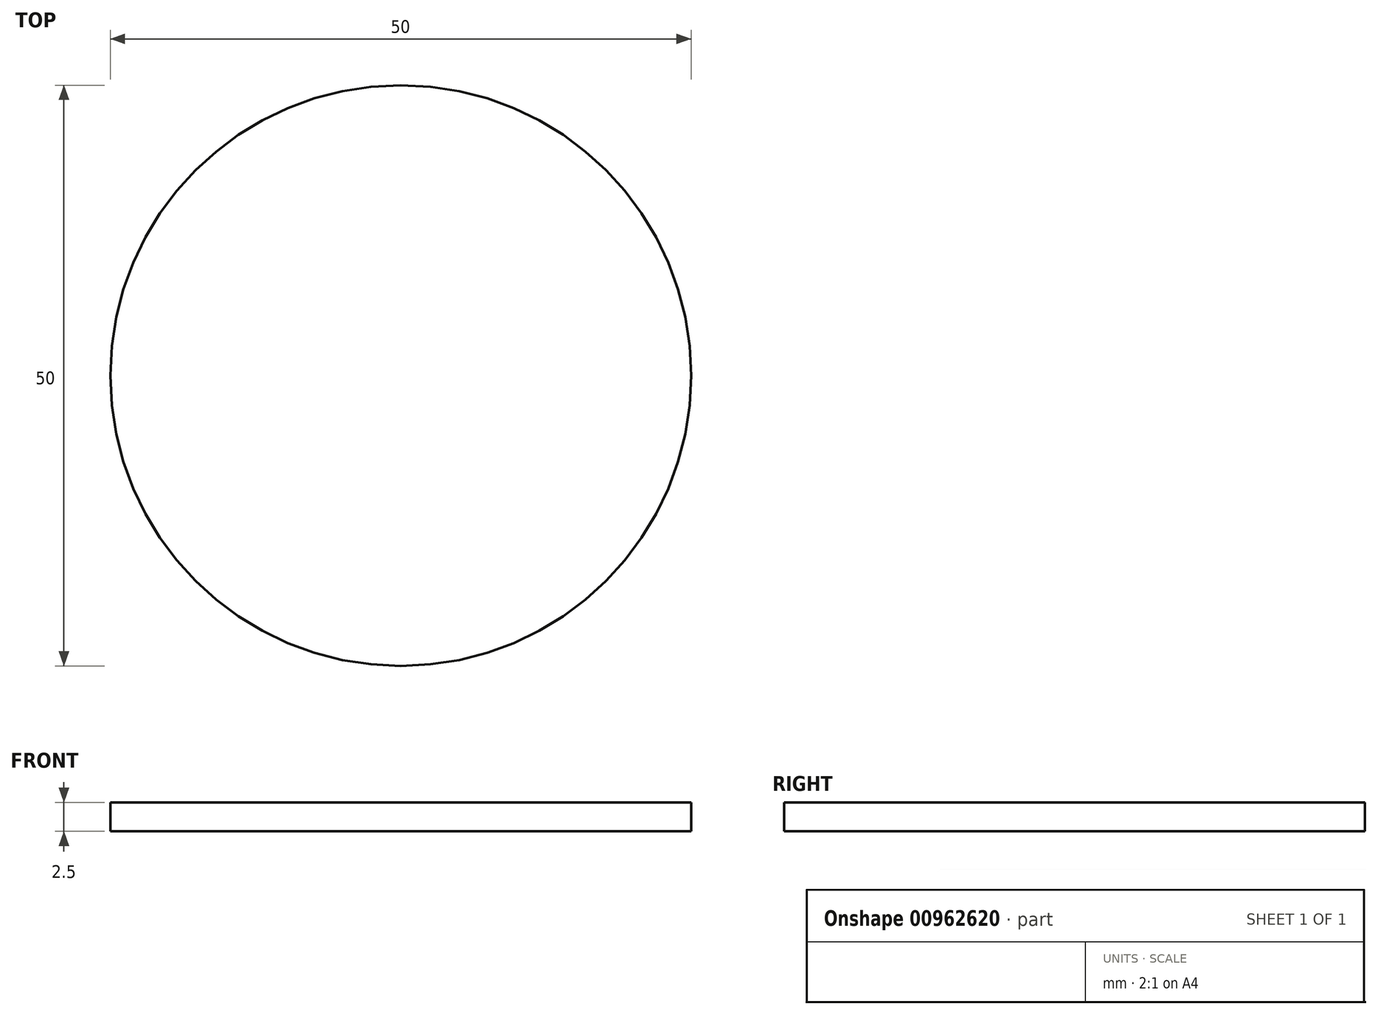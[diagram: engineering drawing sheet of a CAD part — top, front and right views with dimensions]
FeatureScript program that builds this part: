
annotation { "Feature Type Name" : "Feature", "Feature Type Description" : "" }
export const myFeature = defineFeature(function(context is Context, id is Id, definition is map)
    precondition{}
    {
        {
            var Q0;
            Q0=qCreatedBy(makeId("Top.planeOp"),FACE);
            var sketch = newSketch(context, id + "F0", { "sketchPlane" : qUnion([Q0])});
            skCircle(sketch, "E0", {"center": v(0, 0) * mm, "radius": 25 * mm});
            skSolve(sketch);
        }
        {
            var Q0;
            Q0 = qSketchRegion(id + "F0", true);
            extrude(context, id + "F1", {"entities" : qUnion([Q0]), "depth" : 2.5 * mm, "offsetDistance" : 25 * mm});
        }
    });
